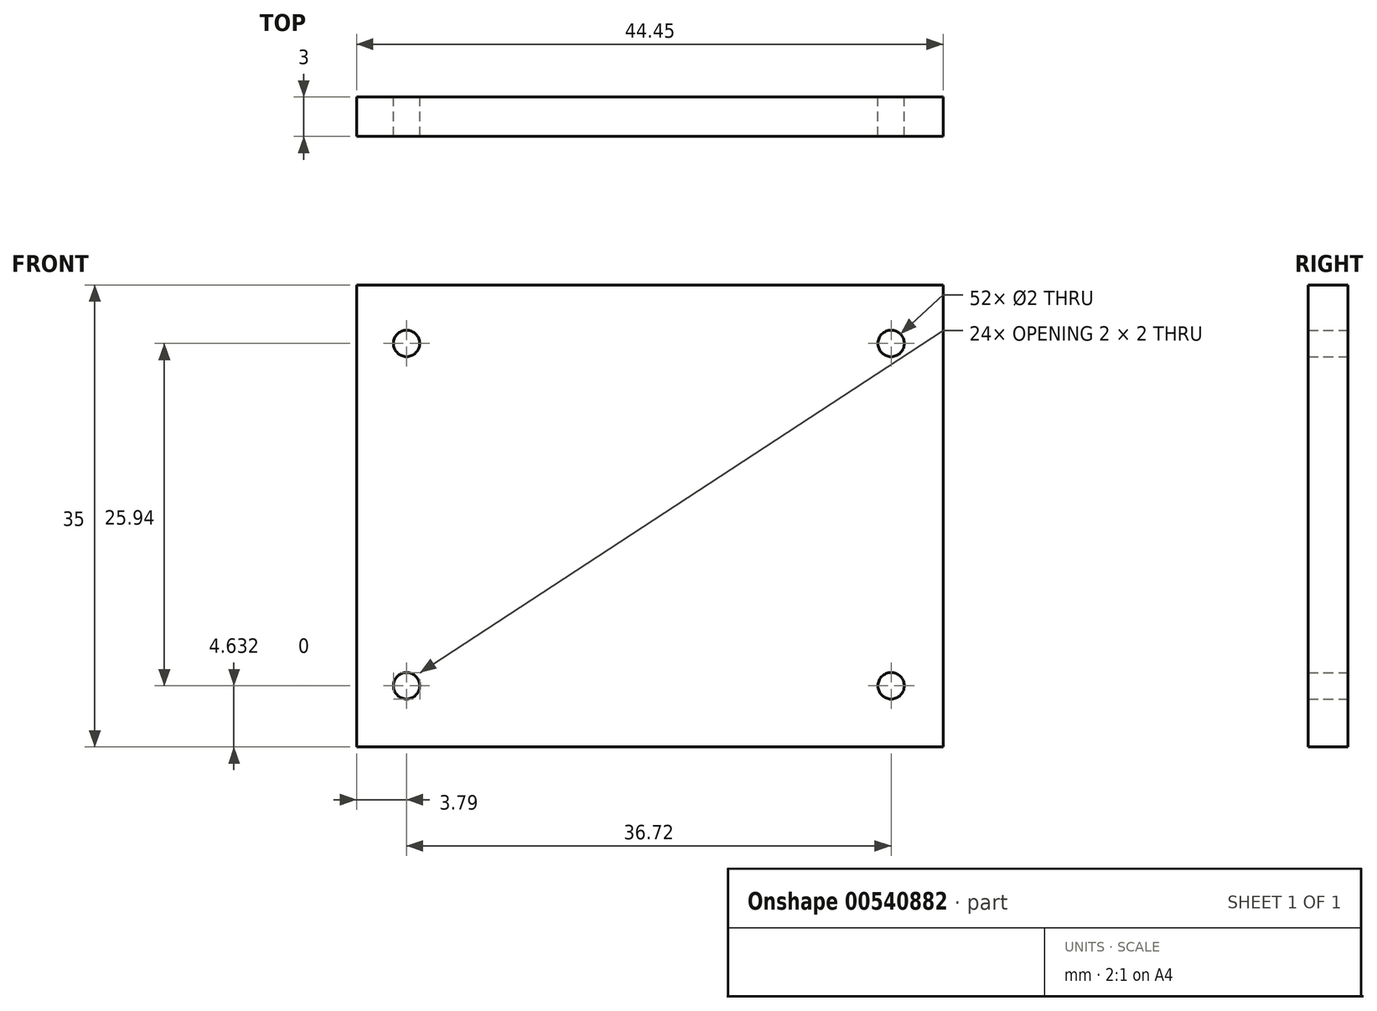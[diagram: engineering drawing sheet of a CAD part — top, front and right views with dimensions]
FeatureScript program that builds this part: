
annotation { "Feature Type Name" : "Feature", "Feature Type Description" : "" }
export const myFeature = defineFeature(function(context is Context, id is Id, definition is map)
    precondition{}
    {
        {
            var Q0;
            Q0=qCreatedBy(makeId("Front.planeOp"),FACE);
            var sketch = newSketch(context, id + "F0", { "sketchPlane" : qUnion([Q0])});
            skLineSegment(sketch, "E0.bottom", {"start": v(0, 0) * mm, "end": v(44.45, 0) * mm});
            skLineSegment(sketch, "E0.top", {"start": v(0, 35) * mm, "end": v(44.45, 35) * mm});
            skLineSegment(sketch, "E0.left", {"start": v(0, 0) * mm, "end": v(0, 35) * mm});
            skLineSegment(sketch, "E0.right", {"start": v(44.45, 0) * mm, "end": v(44.45, 35) * mm});
            skPoint(sketch, "E1", {"position": v(3.79, 30.57) * mm});
            skPoint(sketch, "E2", {"position": v(3.79, 4.63) * mm});
            skPoint(sketch, "E3", {"position": v(40.51, 4.63) * mm});
            skPoint(sketch, "E4", {"position": v(40.51, 30.57) * mm});
            skSolve(sketch);
        }
        {
            var Q0;
            Q0 = qSketchRegion(id + "F0", true);
            extrude(context, id + "F1", {"entities" : qUnion([Q0]), "depth" : 3 * mm, "offsetDistance" : 25.4 * mm});
        }
        {
            var Q0;
            Q0=sQuery(id+"F0.wireOp",VERTEX,"E1");
            var Q1;
            Q1=sQuery(id+"F0.wireOp",VERTEX,"E2");
            var Q2;
            Q2=sQuery(id+"F0.wireOp",VERTEX,"E3");
            var Q3;
            Q3=sQuery(id+"F0.wireOp",VERTEX,"E4");
            var Q4;
            Q4=makeQuery(id+"F1.opExtrude","SWEPT_BODY",BODY,{"disambiguationData":[OSD([sQuery(id+"F0.wireOp",EDGE,"E0.bottom"),sQuery(id+"F0.wireOp",EDGE,"E0.top"),sQuery(id+"F0.wireOp",EDGE,"E0.left"),sQuery(id+"F0.wireOp",EDGE,"E0.right")])]});
            hole(context, id + "F2", {"style" : HoleStyle.SIMPLE, "endStyle" : HoleEndStyle.THROUGH, "oppositeDirection" : true, "holeDiameter" : 2 * mm, "majorDiameter" : 6.35 * mm, "isTappedThrough" : true, "tappedDepth" : 12.7 * mm, "tapClearance" : 3, "locations" : qUnion([Q0, Q1, Q2, Q3]), "scope" : qUnion([Q4])});
        }
    });
